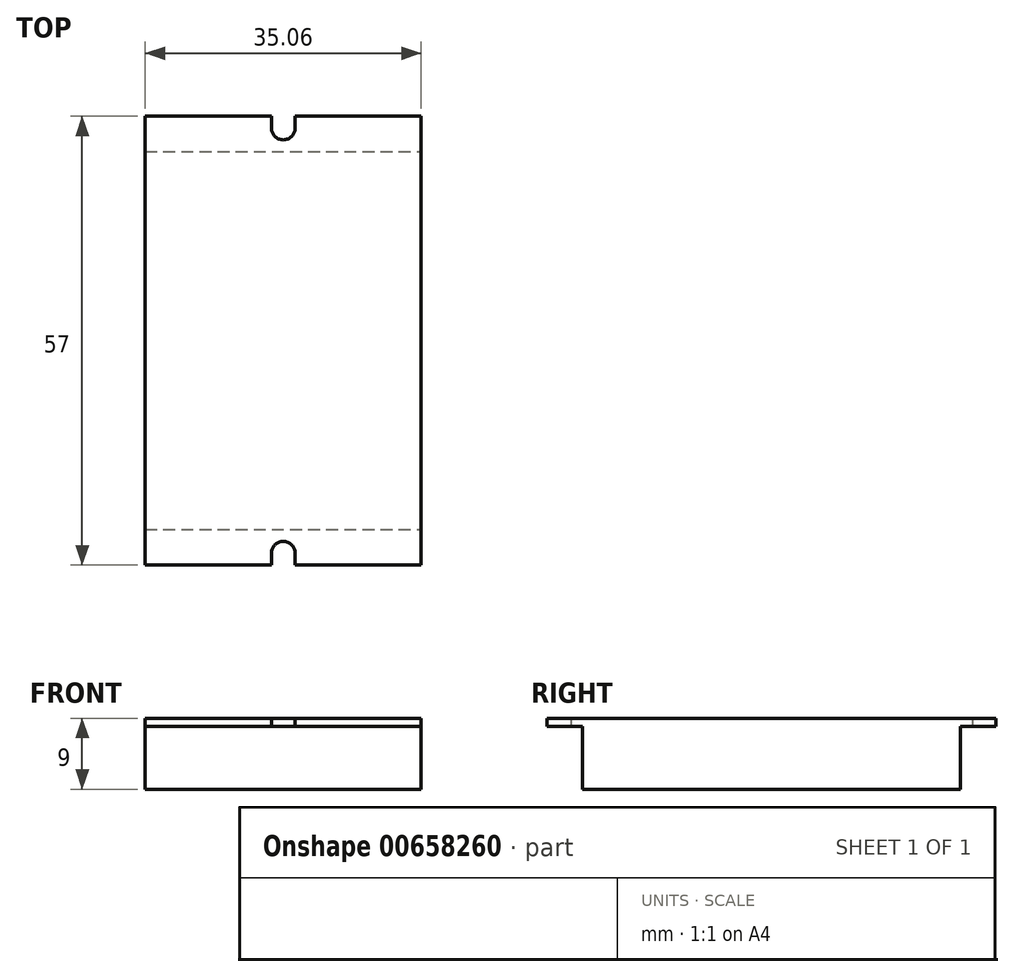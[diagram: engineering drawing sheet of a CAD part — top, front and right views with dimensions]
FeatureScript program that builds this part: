
annotation { "Feature Type Name" : "Feature", "Feature Type Description" : "" }
export const myFeature = defineFeature(function(context is Context, id is Id, definition is map)
    precondition{}
    {
        {
            var Q0;
            Q0=qCreatedBy(makeId("Top.planeOp"),FACE);
            var sketch = newSketch(context, id + "F0", { "sketchPlane" : qUnion([Q0])});
            skLineSegment(sketch, "E0.bottom", {"start": v(-17.53, -28.5) * mm, "end": v(-1.5, -28.5) * mm});
            skLineSegment(sketch, "E0.top", {"start": v(-17.53, 28.5) * mm, "end": v(-1.5, 28.5) * mm});
            skLineSegment(sketch, "E0.left", {"start": v(-17.53, -28.5) * mm, "end": v(-17.53, 28.5) * mm});
            skLineSegment(sketch, "E0.right", {"start": v(17.53, -28.5) * mm, "end": v(17.53, 28.5) * mm});
            skPoint(sketch, "E0.middle", {"position": v(0, 0) * mm});
            skArc(sketch, "E1", {"start": v(1.5, -27) * mm, "mid": v(0, -25.5) * mm, "end": v(-1.5, -27) * mm});
            skArc(sketch, "E2", {"start": v(-1.5, 27) * mm, "mid": v(0, 25.5) * mm, "end": v(1.5, 27) * mm});
            skLineSegment(sketch, "E3", {"start": v(-1.5, 28.5) * mm, "end": v(-1.5, 27) * mm});
            skLineSegment(sketch, "E4", {"start": v(1.5, 28.5) * mm, "end": v(1.5, 27) * mm});
            skLineSegment(sketch, "E5.trimOffspring", {"start": v(1.5, 28.5) * mm, "end": v(17.53, 28.5) * mm});
            skLineSegment(sketch, "E6", {"start": v(-1.5, -28.5) * mm, "end": v(-1.5, -27) * mm});
            skLineSegment(sketch, "E7", {"start": v(1.5, -28.5) * mm, "end": v(1.5, -27) * mm});
            skLineSegment(sketch, "E8.trimOffspring", {"start": v(1.5, -28.5) * mm, "end": v(17.53, -28.5) * mm});
            skLineSegment(sketch, "E9.bottom", {"start": v(-17.53, 24) * mm, "end": v(17.53, 24) * mm});
            skLineSegment(sketch, "E9.top", {"start": v(-17.53, -24) * mm, "end": v(17.53, -24) * mm});
            skLineSegment(sketch, "E9.left", {"start": v(-17.53, 24) * mm, "end": v(-17.53, -24) * mm});
            skLineSegment(sketch, "E9.right", {"start": v(17.53, 24) * mm, "end": v(17.53, -24) * mm});
            skSolve(sketch);
        }
        {
            var Q0;
            {var subQ4=sQuery(id+"F0.wireOp",EDGE,"E0.top");Q0=makeQuery(id+"F0.imprint","IMPRINT",FACE,{"disambiguationData":[TD([[makeQuery(id+"F0.imprint","IMPRINT",EDGE,{"derivedFrom":subQ4}),-1.0]])]});}
            var Q1;
            Q1=makeQuery(id+"F0.imprint","IMPRINT",FACE,{"disambiguationData":[TD([[makeQuery(id+"F0.imprint","IMPRINT",EDGE,{"derivedFrom":sQuery(id+"F0.wireOp",EDGE,"E9.bottom")}),-1.0]])]});
            var Q2;
            {var subQ4=sQuery(id+"F0.wireOp",EDGE,"E0.bottom");Q2=makeQuery(id+"F0.imprint","IMPRINT",FACE,{"disambiguationData":[TD([[makeQuery(id+"F0.imprint","IMPRINT",EDGE,{"derivedFrom":subQ4}),1.0]])]});}
            extrude(context, id + "F1", {"entities" : qUnion([Q0, Q1, Q2]), "depth" : 1 * mm, "offsetDistance" : 25 * mm});
        }
        {
            var Q0;
            Q0=makeQuery(id+"F0.imprint","IMPRINT",FACE,{"disambiguationData":[TD([[makeQuery(id+"F0.imprint","IMPRINT",EDGE,{"derivedFrom":sQuery(id+"F0.wireOp",EDGE,"E9.bottom")}),-1.0]])]});
            extrude(context, id + "F2", {"entities" : qUnion([Q0]), "operationType" : NewBodyOperationType.ADD, "depth" : -8 * mm, "offsetDistance" : 25 * mm});
        }
    });
